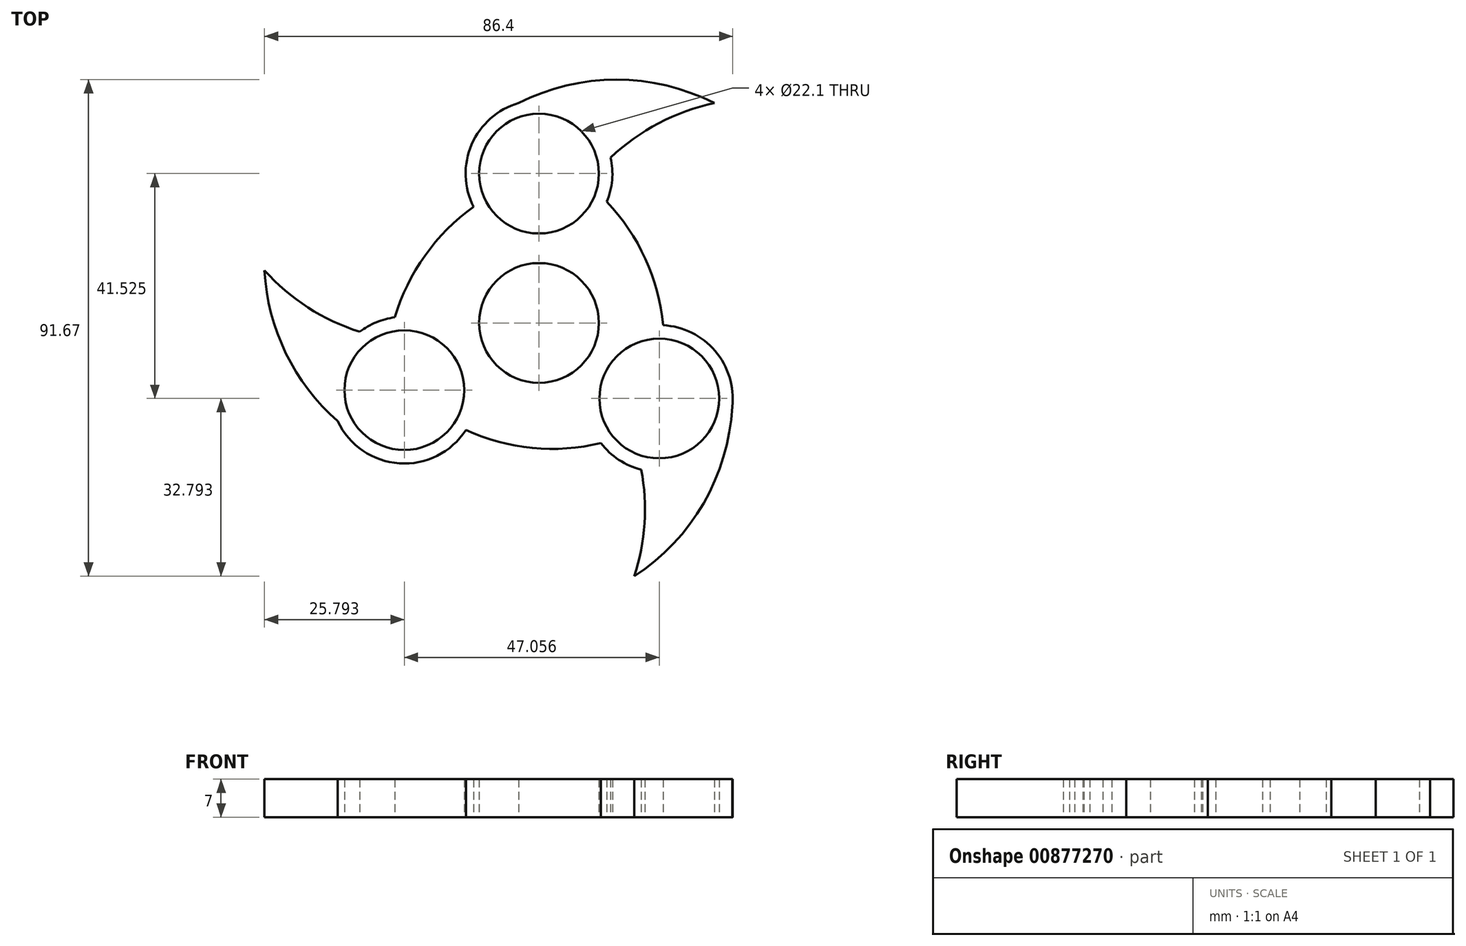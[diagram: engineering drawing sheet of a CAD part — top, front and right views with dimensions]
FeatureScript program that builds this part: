
annotation { "Feature Type Name" : "Feature", "Feature Type Description" : "" }
export const myFeature = defineFeature(function(context is Context, id is Id, definition is map)
    precondition{}
    {
        {
            var Q0;
            Q0=qCreatedBy(makeId("Top.planeOp"),FACE);
            var sketch = newSketch(context, id + "F0", { "sketchPlane" : qUnion([Q0])});
            skCircle(sketch, "E0", {"center": v(0, 0) * mm, "radius": 11.05 * mm});
            skCircle(sketch, "E1", {"center": v(0, 27.57) * mm, "radius": 11.05 * mm});
            skArc(sketch, "E2", {"start": v(12.51, 22.37) * mm, "mid": v(-0.52, 41.1) * mm, "end": v(-12.07, 21.41) * mm});
            skArc(sketch, "E3.1.0", {"start": v(-26.62, 1.03) * mm, "mid": v(-36.33, -19.63) * mm, "end": v(-13.5, -19.79) * mm});
            skCircle(sketch, "E3.1.1", {"center": v(-24.87, -12.41) * mm, "radius": 11.05 * mm});
            skArc(sketch, "E3.2.0", {"start": v(11.43, -22.2) * mm, "mid": v(34.18, -20.27) * mm, "end": v(22.9, -0.43) * mm});
            skCircle(sketch, "E3.2.1", {"center": v(22.19, -13.96) * mm, "radius": 11.05 * mm});
            skPoint(sketch, "E3.center", {"position": v(-0.9, 0.4) * mm});
            skArc(sketch, "E4", {"start": v(32.35, 40.58) * mm, "mid": v(14.3, 44.92) * mm, "end": v(-3.77, 40.58) * mm});
            skArc(sketch, "E5", {"start": v(32.35, 40.58) * mm, "mid": v(22.1, 36.89) * mm, "end": v(13.22, 30.54) * mm});
            skArc(sketch, "E6.1.0", {"start": v(-50.66, 9.7) * mm, "mid": v(-46.72, -5.6) * mm, "end": v(-37.14, -18.15) * mm});
            skArc(sketch, "E6.1.1", {"start": v(-50.66, 9.7) * mm, "mid": v(-42.63, 2.85) * mm, "end": v(-33.09, -1.64) * mm});
            skArc(sketch, "E6.2.0", {"start": v(17.6, -46.75) * mm, "mid": v(30.38, -33.28) * mm, "end": v(35.65, -15.47) * mm});
            skArc(sketch, "E6.2.1", {"start": v(17.6, -46.75) * mm, "mid": v(19.47, -37) * mm, "end": v(18.87, -27.1) * mm});
            skPoint(sketch, "E6.center", {"position": v(-0.24, 1.18) * mm});
            skArc(sketch, "E7", {"start": v(-12.07, 21.41) * mm, "mid": v(-21.06, 12.44) * mm, "end": v(-26.62, 1.03) * mm});
            skArc(sketch, "E8.1.0", {"start": v(-13.5, -19.79) * mm, "mid": v(-1.24, -23.08) * mm, "end": v(11.43, -22.2) * mm});
            skArc(sketch, "E8.2.0", {"start": v(22.9, -0.43) * mm, "mid": v(19.62, 11.84) * mm, "end": v(12.51, 22.37) * mm});
            skPoint(sketch, "E9.orphan", {"position": v(-32.6, -21.58) * mm});
            skPoint(sketch, "E10.orphan", {"position": v(18.46, -25.16) * mm});
            skPoint(sketch, "E11.orphan", {"position": v(-32.4, -1.85) * mm});
            skSolve(sketch);
        }
        {
            var Q0;
            Q0 = qSketchRegion(id + "F0", true);
            extrude(context, id + "F1", {"entities" : qUnion([Q0]), "depth" : 7 * mm, "offsetDistance" : 25 * mm});
        }
    });
